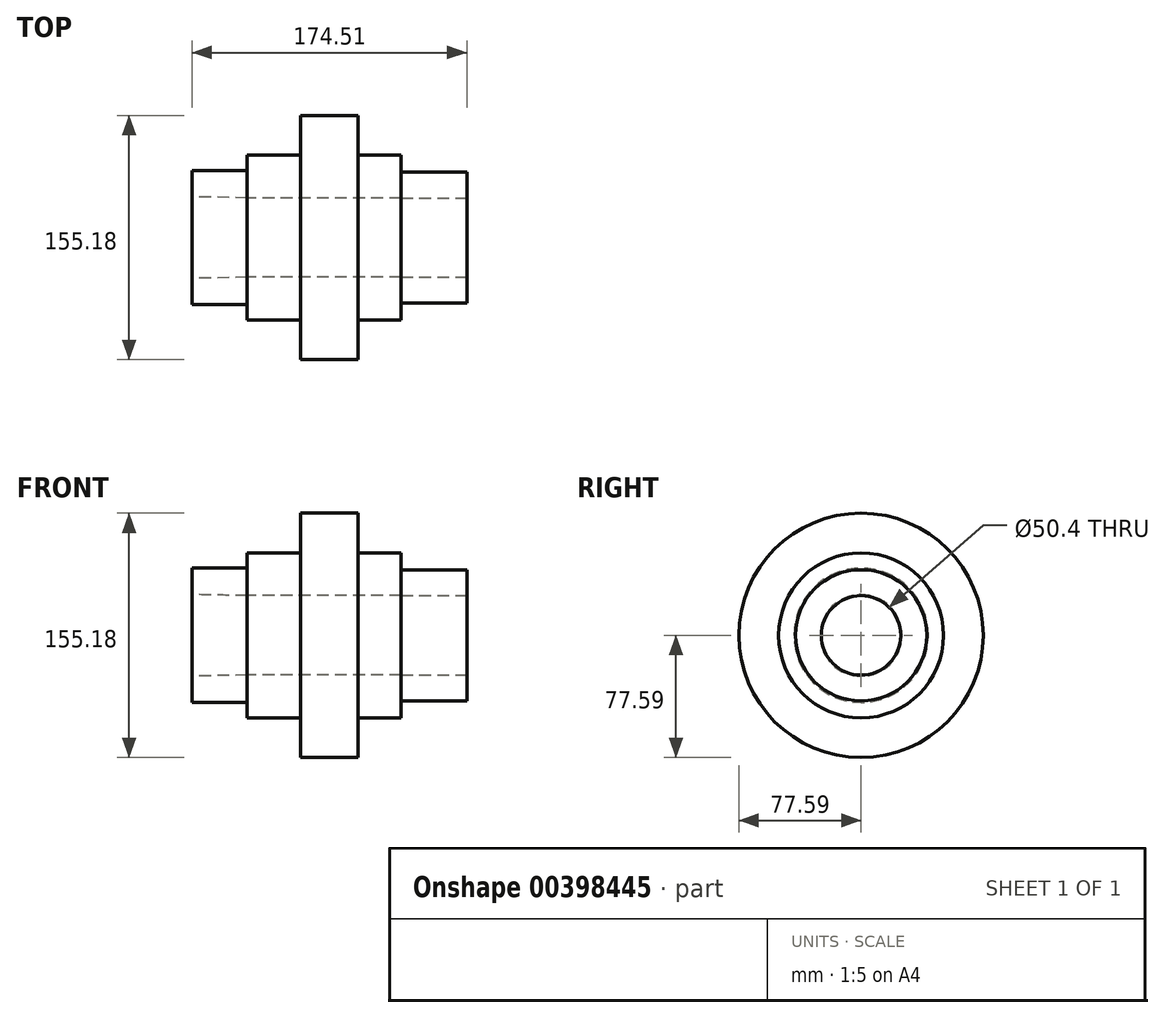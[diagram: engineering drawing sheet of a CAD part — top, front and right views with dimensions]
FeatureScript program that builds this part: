
annotation { "Feature Type Name" : "Feature", "Feature Type Description" : "" }
export const myFeature = defineFeature(function(context is Context, id is Id, definition is map)
    precondition{}
    {
        {
            var Q0;
            Q0=qCreatedBy(makeId("Front.planeOp"),FACE);
            var sketch = newSketch(context, id + "F0", { "sketchPlane" : qUnion([Q0])});
            skLineSegment(sketch, "E0.top", {"start": v(-35.56, 0) * mm, "end": v(46.07, 0) * mm});
            skLineSegment(sketch, "E0.right", {"start": v(46.07, 36.95) * mm, "end": v(46.07, 0) * mm});
            skLineSegment(sketch, "E1", {"start": v(-140.08, 27.37) * mm, "end": v(-140.08, 0) * mm});
            skLineSegment(sketch, "E2", {"start": v(-140.08, 0) * mm, "end": v(-103.28, 0) * mm});
            skLineSegment(sketch, "E3", {"start": v(-103.28, 0) * mm, "end": v(-103.28, -14.69) * mm});
            skLineSegment(sketch, "E4.top", {"start": v(-62.77, 25.2) * mm, "end": v(34.94, 25.2) * mm});
            skLineSegment(sketch, "E5", {"start": v(-84.42, 0) * mm, "end": v(107.92, 0) * mm, "construction": true});
            skLineSegment(sketch, "E6", {"start": v(-62.77, 52.41) * mm, "end": v(-28.97, 52.41) * mm});
            skLineSegment(sketch, "E7", {"start": v(-28.97, 52.41) * mm, "end": v(-28.97, 77.6) * mm});
            skLineSegment(sketch, "E8", {"start": v(-28.97, 77.6) * mm, "end": v(7.6, 77.6) * mm});
            skLineSegment(sketch, "E9", {"start": v(7.6, 77.6) * mm, "end": v(7.6, 52.41) * mm});
            skLineSegment(sketch, "E10", {"start": v(7.6, 52.41) * mm, "end": v(34.94, 52.41) * mm});
            skLineSegment(sketch, "E11", {"start": v(-62.77, 52.41) * mm, "end": v(-62.77, 42.66) * mm});
            skLineSegment(sketch, "E12", {"start": v(-62.77, 42.66) * mm, "end": v(-97.83, 42.66) * mm});
            skLineSegment(sketch, "E13", {"start": v(-97.83, 42.66) * mm, "end": v(-97.83, 25.94) * mm});
            skLineSegment(sketch, "E14", {"start": v(-97.83, 25.94) * mm, "end": v(-62.77, 25.2) * mm});
            skLineSegment(sketch, "E15", {"start": v(34.94, 52.41) * mm, "end": v(34.94, 41.69) * mm});
            skLineSegment(sketch, "E16", {"start": v(34.94, 41.69) * mm, "end": v(76.68, 41.69) * mm});
            skLineSegment(sketch, "E17", {"start": v(76.68, 41.69) * mm, "end": v(76.68, 25.22) * mm});
            skLineSegment(sketch, "E18", {"start": v(76.68, 25.22) * mm, "end": v(34.94, 25.2) * mm});
            skSolve(sketch);
        }
        {
            var Q0;
            Q0=makeQuery(id+"F0.imprint","IMPRINT",FACE,{"disambiguationData":[TD([[makeQuery(id+"F0.imprint","IMPRINT",EDGE,{"derivedFrom":sQuery(id+"F0.wireOp",EDGE,"E4.top")}),1.0]])]});
            var Q1;
            Q1=sQuery(id+"F0.wireOp",EDGE,"E5");
            revolve(context, id + "F1", {"entities" : qUnion([Q0]), "axis" : qUnion([Q1]), "revolveType" : RevolveType.FULL});
        }
    });
